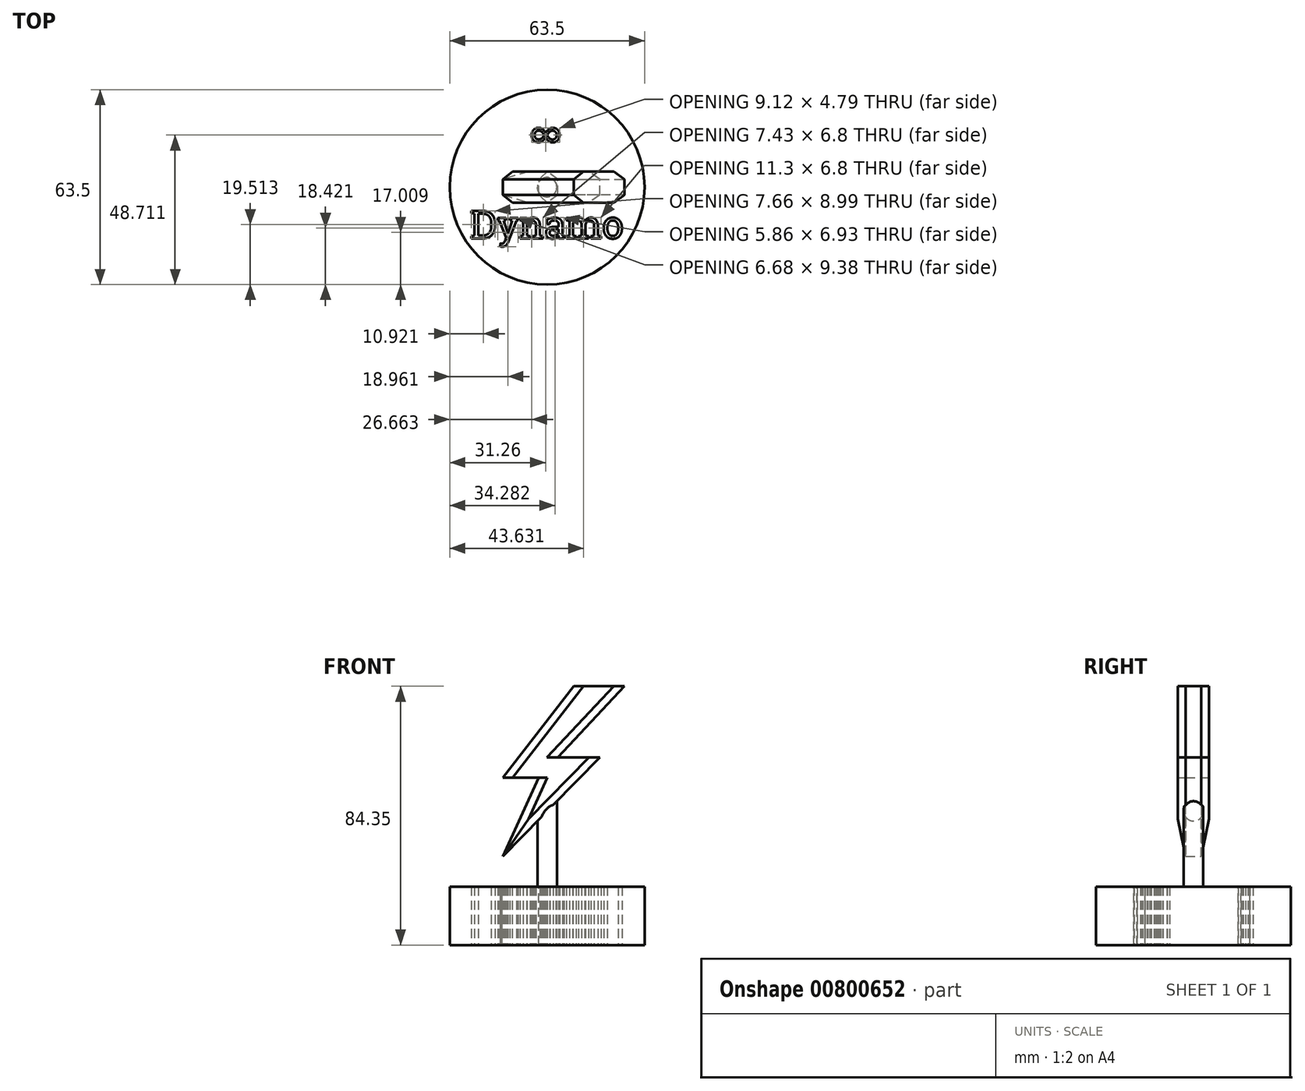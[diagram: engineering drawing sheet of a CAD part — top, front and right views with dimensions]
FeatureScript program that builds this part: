
annotation { "Feature Type Name" : "Feature", "Feature Type Description" : "" }
export const myFeature = defineFeature(function(context is Context, id is Id, definition is map)
    precondition{}
    {
        {
            var Q0;
            Q0=qCreatedBy(makeId("Top.planeOp"),FACE);
            var sketch = newSketch(context, id + "F0", { "sketchPlane" : qUnion([Q0])});
            skCircle(sketch, "E0", {"center": v(0, 0) * mm, "radius": 31.75 * mm});
            skSolve(sketch);
        }
        {
            var Q0;
            Q0 = qSketchRegion(id + "F0", true);
            extrude(context, id + "F1", {"entities" : qUnion([Q0]), "depth" : 19.05 * mm, "offsetDistance" : 25.4 * mm});
        }
        {
            var Q0;
            Q0=qCreatedBy(makeId("Top.planeOp"),FACE);
            var sketch = newSketch(context, id + "F2", { "sketchPlane" : qUnion([Q0])});
            skCircle(sketch, "E1", {"center": v(0, 0) * mm, "radius": 3.16 * mm});
            skSolve(sketch);
        }
        {
            var Q0;
            Q0 = qSketchRegion(id + "F2", true);
            extrude(context, id + "F3", {"entities" : qUnion([Q0]), "operationType" : NewBodyOperationType.ADD, "depth" : 50.8 * mm, "offsetDistance" : 25.4 * mm});
        }
        {
            var Q0;
            Q0=qCreatedBy(makeId("Front.planeOp"),FACE);
            var sketch = newSketch(context, id + "F4", { "sketchPlane" : qUnion([Q0])});
            skLineSegment(sketch, "E2", {"start": v(-6.6, 36.88) * mm, "end": v(17.13, 61.2) * mm});
            skLineSegment(sketch, "E3", {"start": v(17.13, 61.2) * mm, "end": v(3.46, 61.2) * mm});
            skLineSegment(sketch, "E4", {"start": v(3.46, 61.2) * mm, "end": v(25.24, 84.35) * mm});
            skLineSegment(sketch, "E5", {"start": v(-6.6, 36.88) * mm, "end": v(-14.43, 28.87) * mm});
            skLineSegment(sketch, "E6", {"start": v(-14.43, 28.87) * mm, "end": v(-2.7, 54.52) * mm});
            skLineSegment(sketch, "E7", {"start": v(-2.7, 54.52) * mm, "end": v(-14.43, 54.52) * mm});
            skLineSegment(sketch, "E8", {"start": v(-14.43, 54.52) * mm, "end": v(8.67, 84.35) * mm});
            skLineSegment(sketch, "E9", {"start": v(8.67, 84.35) * mm, "end": v(25.24, 84.35) * mm});
            skSolve(sketch);
        }
        {
            var Q0;
            Q0 = qSketchRegion(id + "F4", true);
            extrude(context, id + "F5", {"entities" : qUnion([Q0]), "operationType" : NewBodyOperationType.ADD, "depth" : 5.08 * mm, "offsetDistance" : 25.4 * mm, "hasSecondDirection" : true, "secondDirectionOppositeDirection" : true, "secondDirectionDepth" : 5.08 * mm});
        }
        {
            var Q0;
            Q0=makeQuery(id+"F5.opExtrude","CAP_EDGE",EDGE,{"disambiguationData":[OSD([sQuery(id+"F4.wireOp",EDGE,"E8")])],"isStart":false});
            var Q1;
            Q1=makeQuery(id+"F5.opExtrude","CAP_EDGE",EDGE,{"disambiguationData":[OSD([sQuery(id+"F4.wireOp",EDGE,"E6")])],"isStart":false});
            var Q2;
            Q2=makeQuery(id+"F5.opExtrude","CAP_EDGE",EDGE,{"disambiguationData":[OSD([sQuery(id+"F4.wireOp",EDGE,"E2"),sQuery(id+"F4.wireOp",EDGE,"E5")])],"isStart":false});
            var Q3;
            Q3=makeQuery(id+"F5.opExtrude","CAP_EDGE",EDGE,{"disambiguationData":[OSD([sQuery(id+"F4.wireOp",EDGE,"E4")])],"isStart":false});
            var Q4;
            Q4=makeQuery(id+"F5.opExtrude","CAP_EDGE",EDGE,{"disambiguationData":[OSD([sQuery(id+"F4.wireOp",EDGE,"E6")])],"isStart":true});
            var Q5;
            Q5=makeQuery(id+"F5.opExtrude","CAP_EDGE",EDGE,{"disambiguationData":[OSD([sQuery(id+"F4.wireOp",EDGE,"E2"),sQuery(id+"F4.wireOp",EDGE,"E5")])],"isStart":true});
            var Q6;
            Q6=makeQuery(id+"F5.opExtrude","CAP_EDGE",EDGE,{"disambiguationData":[OSD([sQuery(id+"F4.wireOp",EDGE,"E8")])],"isStart":true});
            var Q7;
            Q7=makeQuery(id+"F5.opExtrude","CAP_EDGE",EDGE,{"disambiguationData":[OSD([sQuery(id+"F4.wireOp",EDGE,"E4")])],"isStart":true});
            chamfer(context, id + "F6", {"entities" : qUnion([Q0, Q1, Q2, Q3, Q4, Q5, Q6, Q7]), "width" : 2.54 * mm, "tangentPropagation" : true});
        }
        {
            var Q0;
            Q0=qCreatedBy(makeId("Top.planeOp"),FACE);
            var sketch = newSketch(context, id + "F7", { "sketchPlane" : qUnion([Q0])});
            skText(sketch, "E10", { "text": "Dynamo", "fontName": "RobotoSlab-Regular.ttf"});
            const initialGuessF7  = {"E10": [-0.0251, -0.01673, 1, 0, 0.0091]};
            skSetInitialGuess(sketch, initialGuessF7);
            skSolve(sketch);
        }
        {
            var Q0;
            Q0 = qSketchRegion(id + "F7", true);
            extrude(context, id + "F8", {"entities" : qUnion([Q0]), "operationType" : NewBodyOperationType.REMOVE, "depth" : 67.82 * mm, "offsetDistance" : 25.4 * mm});
        }
        {
            var Q0;
            Q0=qCreatedBy(makeId("Top.planeOp"),FACE);
            var sketch = newSketch(context, id + "F9", { "sketchPlane" : qUnion([Q0])});
            skText(sketch, "E11", { "text": "∞\n", "fontName": "OpenSans-Regular.ttf"});
            const initialGuessF9  = {"E11": [-0.00595, 0.01152, 1, 0, 0.01115]};
            skSetInitialGuess(sketch, initialGuessF9);
            skSolve(sketch);
        }
        {
            var Q0;
            Q0 = qSketchRegion(id + "F9", true);
            extrude(context, id + "F10", {"entities" : qUnion([Q0]), "operationType" : NewBodyOperationType.REMOVE, "depth" : 263.14 * mm, "offsetDistance" : 25.4 * mm});
        }
    });
